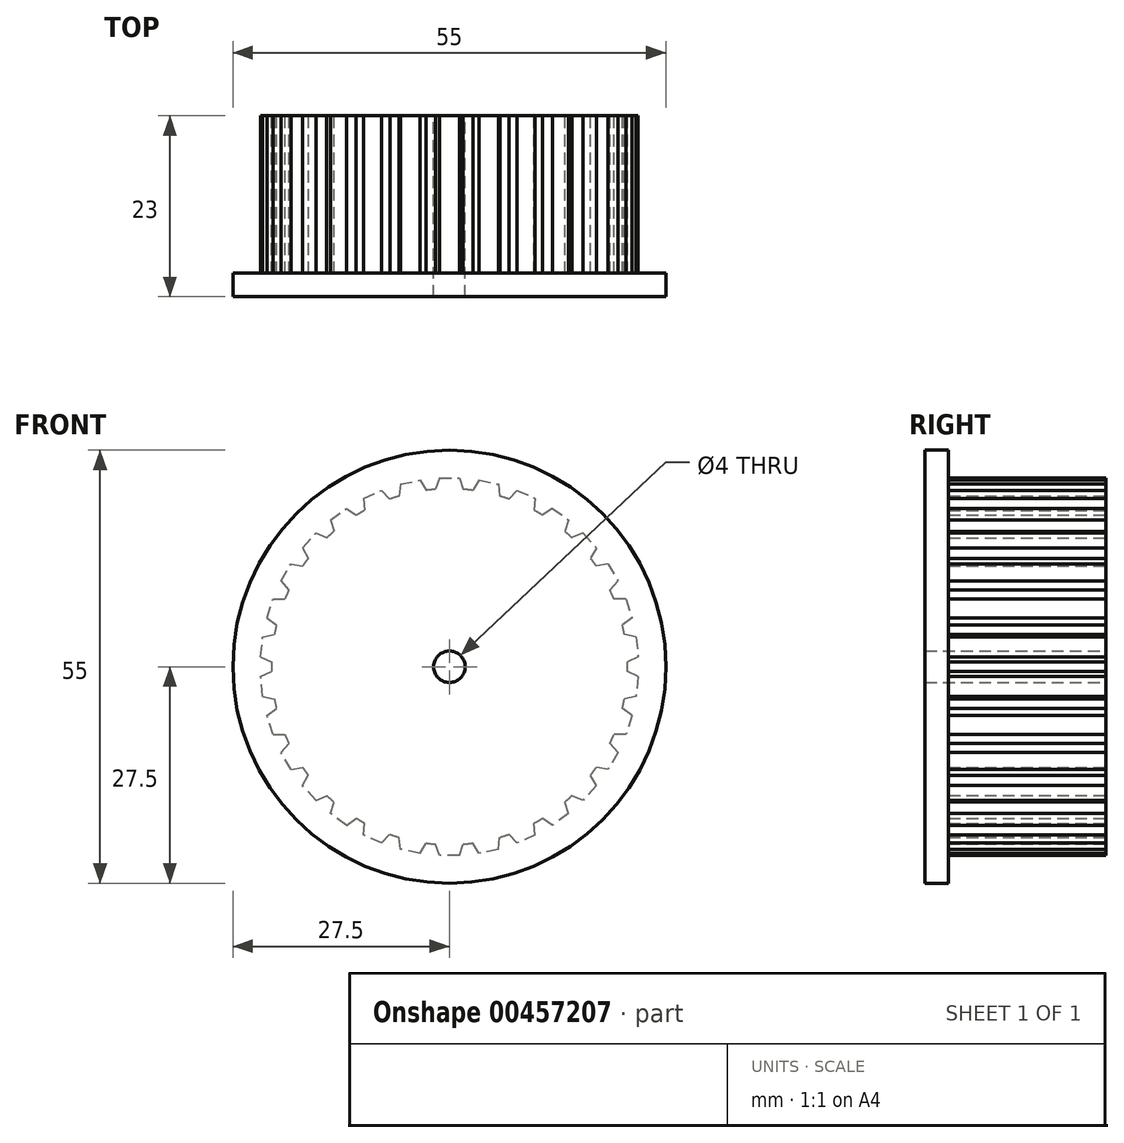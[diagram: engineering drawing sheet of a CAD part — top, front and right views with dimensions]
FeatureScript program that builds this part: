
annotation { "Feature Type Name" : "Feature", "Feature Type Description" : "" }
export const myFeature = defineFeature(function(context is Context, id is Id, definition is map)
    precondition{}
    {
        {
            var Q0;
            Q0=qCreatedBy(makeId("Front.planeOp"),FACE);
            var sketch = newSketch(context, id + "F0", { "sketchPlane" : qUnion([Q0])});
            skCircle(sketch, "E0", {"center": v(0, 0) * mm, "radius": 24 * mm, "construction": true});
            skLineSegment(sketch, "E1", {"start": v(0, 24) * mm, "end": v(0, 22.6) * mm, "construction": true});
            skCircle(sketch, "E2", {"center": v(0, 0) * mm, "radius": 22.6 * mm});
            skLineSegment(sketch, "E3", {"start": v(0, 0) * mm, "end": v(-1.26, 23.97) * mm, "construction": true});
            skLineSegment(sketch, "E4", {"start": v(0, 0) * mm, "end": v(-2.5, 23.87) * mm, "construction": true});
            skLineSegment(sketch, "E5.MirrorCS", {"start": v(0, 0) * mm, "end": v(1.26, 23.97) * mm, "construction": true});
            skLineSegment(sketch, "E6.MirrorCS", {"start": v(0, 0) * mm, "end": v(2.5, 23.87) * mm, "construction": true});
            skLineSegment(sketch, "E7", {"start": v(-1.26, 23.97) * mm, "end": v(1.26, 23.97) * mm});
            skLineSegment(sketch, "E8", {"start": v(-1.26, 23.97) * mm, "end": v(-1.75, 22.53) * mm});
            skLineSegment(sketch, "E9.MirrorCS", {"start": v(1.26, 23.97) * mm, "end": v(1.75, 22.53) * mm});
            skLineSegment(sketch, "E10.1.0", {"start": v(-6.21, 23.18) * mm, "end": v(-6.4, 21.68) * mm});
            skLineSegment(sketch, "E10.1.1", {"start": v(-6.21, 23.18) * mm, "end": v(-3.75, 23.7) * mm});
            skLineSegment(sketch, "E10.1.2", {"start": v(-3.75, 23.7) * mm, "end": v(-2.97, 22.4) * mm});
            skLineSegment(sketch, "E10.2.0", {"start": v(-10.9, 21.38) * mm, "end": v(-10.76, 19.87) * mm});
            skLineSegment(sketch, "E10.2.1", {"start": v(-10.9, 21.38) * mm, "end": v(-8.6, 22.4) * mm});
            skLineSegment(sketch, "E10.2.2", {"start": v(-8.6, 22.4) * mm, "end": v(-7.57, 21.3) * mm});
            skLineSegment(sketch, "E10.3.0", {"start": v(-15.1, 18.65) * mm, "end": v(-14.66, 17.2) * mm});
            skLineSegment(sketch, "E10.3.1", {"start": v(-15.1, 18.65) * mm, "end": v(-13.07, 20.13) * mm});
            skLineSegment(sketch, "E10.3.2", {"start": v(-13.07, 20.13) * mm, "end": v(-11.83, 19.26) * mm});
            skLineSegment(sketch, "E10.4.0", {"start": v(-18.65, 15.1) * mm, "end": v(-17.92, 13.78) * mm});
            skLineSegment(sketch, "E10.4.1", {"start": v(-18.65, 15.1) * mm, "end": v(-16.97, 16.97) * mm});
            skLineSegment(sketch, "E10.4.2", {"start": v(-16.97, 16.97) * mm, "end": v(-15.57, 16.38) * mm});
            skLineSegment(sketch, "E10.5.0", {"start": v(-21.38, 10.9) * mm, "end": v(-20.39, 9.75) * mm});
            skLineSegment(sketch, "E10.5.1", {"start": v(-21.38, 10.9) * mm, "end": v(-20.13, 13.07) * mm});
            skLineSegment(sketch, "E10.5.2", {"start": v(-20.13, 13.07) * mm, "end": v(-18.64, 12.78) * mm});
            skLineSegment(sketch, "E10.6.0", {"start": v(-23.18, 6.21) * mm, "end": v(-21.97, 5.3) * mm});
            skLineSegment(sketch, "E10.6.1", {"start": v(-23.18, 6.21) * mm, "end": v(-22.4, 8.6) * mm});
            skLineSegment(sketch, "E10.6.2", {"start": v(-22.4, 8.6) * mm, "end": v(-20.89, 8.63) * mm});
            skLineSegment(sketch, "E10.7.0", {"start": v(-23.97, 1.26) * mm, "end": v(-22.6, 0.61) * mm});
            skLineSegment(sketch, "E10.7.1", {"start": v(-23.97, 1.26) * mm, "end": v(-23.7, 3.75) * mm});
            skLineSegment(sketch, "E10.7.2", {"start": v(-23.7, 3.75) * mm, "end": v(-22.23, 4.1) * mm});
            skLineSegment(sketch, "E10.8.0", {"start": v(-23.7, -3.75) * mm, "end": v(-22.23, -4.1) * mm});
            skLineSegment(sketch, "E10.8.1", {"start": v(-23.7, -3.75) * mm, "end": v(-23.97, -1.26) * mm});
            skLineSegment(sketch, "E10.8.2", {"start": v(-23.97, -1.26) * mm, "end": v(-22.6, -0.61) * mm});
            skLineSegment(sketch, "E10.9.0", {"start": v(-22.4, -8.6) * mm, "end": v(-20.89, -8.63) * mm});
            skLineSegment(sketch, "E10.9.1", {"start": v(-22.4, -8.6) * mm, "end": v(-23.18, -6.21) * mm});
            skLineSegment(sketch, "E10.9.2", {"start": v(-23.18, -6.21) * mm, "end": v(-21.97, -5.3) * mm});
            skLineSegment(sketch, "E11", {"start": v(0, 0) * mm, "end": v(0, 24) * mm, "construction": true});
            skLineSegment(sketch, "E12.2.10.0", {"start": v(-20.13, -13.07) * mm, "end": v(-18.64, -12.78) * mm});
            skLineSegment(sketch, "E12.3.10.0", {"start": v(-20.13, -13.07) * mm, "end": v(-21.38, -10.9) * mm});
            skLineSegment(sketch, "E12.6.10.0", {"start": v(-21.38, -10.9) * mm, "end": v(-20.39, -9.75) * mm});
            skLineSegment(sketch, "E12.2.11.0", {"start": v(-16.97, -16.97) * mm, "end": v(-15.57, -16.38) * mm});
            skLineSegment(sketch, "E12.3.11.0", {"start": v(-16.97, -16.97) * mm, "end": v(-18.65, -15.1) * mm});
            skLineSegment(sketch, "E12.6.11.0", {"start": v(-18.65, -15.1) * mm, "end": v(-17.92, -13.78) * mm});
            skLineSegment(sketch, "E12.2.12.0", {"start": v(-13.07, -20.13) * mm, "end": v(-11.83, -19.26) * mm});
            skLineSegment(sketch, "E12.3.12.0", {"start": v(-13.07, -20.13) * mm, "end": v(-15.1, -18.65) * mm});
            skLineSegment(sketch, "E12.6.12.0", {"start": v(-15.1, -18.65) * mm, "end": v(-14.66, -17.2) * mm});
            skLineSegment(sketch, "E12.2.13.0", {"start": v(-8.6, -22.4) * mm, "end": v(-7.57, -21.3) * mm});
            skLineSegment(sketch, "E12.3.13.0", {"start": v(-8.6, -22.4) * mm, "end": v(-10.9, -21.38) * mm});
            skLineSegment(sketch, "E12.6.13.0", {"start": v(-10.9, -21.38) * mm, "end": v(-10.76, -19.87) * mm});
            skLineSegment(sketch, "E12.2.14.0", {"start": v(-3.75, -23.7) * mm, "end": v(-2.97, -22.4) * mm});
            skLineSegment(sketch, "E12.3.14.0", {"start": v(-3.75, -23.7) * mm, "end": v(-6.21, -23.18) * mm});
            skLineSegment(sketch, "E12.6.14.0", {"start": v(-6.21, -23.18) * mm, "end": v(-6.4, -21.68) * mm});
            skLineSegment(sketch, "E12.2.15.0", {"start": v(1.26, -23.97) * mm, "end": v(1.75, -22.53) * mm});
            skLineSegment(sketch, "E12.3.15.0", {"start": v(1.26, -23.97) * mm, "end": v(-1.26, -23.97) * mm});
            skLineSegment(sketch, "E12.6.15.0", {"start": v(-1.26, -23.97) * mm, "end": v(-1.75, -22.53) * mm});
            skLineSegment(sketch, "E12.2.16.0", {"start": v(6.21, -23.18) * mm, "end": v(6.4, -21.68) * mm});
            skLineSegment(sketch, "E12.3.16.0", {"start": v(6.21, -23.18) * mm, "end": v(3.75, -23.7) * mm});
            skLineSegment(sketch, "E12.6.16.0", {"start": v(3.75, -23.7) * mm, "end": v(2.97, -22.4) * mm});
            skLineSegment(sketch, "E12.2.17.0", {"start": v(10.9, -21.38) * mm, "end": v(10.76, -19.87) * mm});
            skLineSegment(sketch, "E12.3.17.0", {"start": v(10.9, -21.38) * mm, "end": v(8.6, -22.4) * mm});
            skLineSegment(sketch, "E12.6.17.0", {"start": v(8.6, -22.4) * mm, "end": v(7.57, -21.3) * mm});
            skLineSegment(sketch, "E12.2.18.0", {"start": v(15.1, -18.65) * mm, "end": v(14.66, -17.2) * mm});
            skLineSegment(sketch, "E12.3.18.0", {"start": v(15.1, -18.65) * mm, "end": v(13.07, -20.13) * mm});
            skLineSegment(sketch, "E12.6.18.0", {"start": v(13.07, -20.13) * mm, "end": v(11.83, -19.26) * mm});
            skLineSegment(sketch, "E12.2.19.0", {"start": v(18.65, -15.1) * mm, "end": v(17.92, -13.78) * mm});
            skLineSegment(sketch, "E12.3.19.0", {"start": v(18.65, -15.1) * mm, "end": v(16.97, -16.97) * mm});
            skLineSegment(sketch, "E12.6.19.0", {"start": v(16.97, -16.97) * mm, "end": v(15.57, -16.38) * mm});
            skCircle(sketch, "E13", {"center": v(0, 0) * mm, "radius": 2 * mm});
            skLineSegment(sketch, "E14.2.20.0", {"start": v(21.38, -10.9) * mm, "end": v(20.39, -9.75) * mm});
            skLineSegment(sketch, "E14.3.20.0", {"start": v(21.38, -10.9) * mm, "end": v(20.13, -13.07) * mm});
            skLineSegment(sketch, "E14.6.20.0", {"start": v(20.13, -13.07) * mm, "end": v(18.64, -12.78) * mm});
            skLineSegment(sketch, "E14.2.21.0", {"start": v(23.18, -6.21) * mm, "end": v(21.97, -5.3) * mm});
            skLineSegment(sketch, "E14.3.21.0", {"start": v(23.18, -6.21) * mm, "end": v(22.4, -8.6) * mm});
            skLineSegment(sketch, "E14.6.21.0", {"start": v(22.4, -8.6) * mm, "end": v(20.89, -8.63) * mm});
            skLineSegment(sketch, "E14.2.22.0", {"start": v(23.97, -1.26) * mm, "end": v(22.6, -0.61) * mm});
            skLineSegment(sketch, "E14.3.22.0", {"start": v(23.97, -1.26) * mm, "end": v(23.7, -3.75) * mm});
            skLineSegment(sketch, "E14.6.22.0", {"start": v(23.7, -3.75) * mm, "end": v(22.23, -4.1) * mm});
            skLineSegment(sketch, "E14.2.23.0", {"start": v(23.7, 3.75) * mm, "end": v(22.23, 4.1) * mm});
            skLineSegment(sketch, "E14.3.23.0", {"start": v(23.7, 3.75) * mm, "end": v(23.97, 1.26) * mm});
            skLineSegment(sketch, "E14.6.23.0", {"start": v(23.97, 1.26) * mm, "end": v(22.6, 0.61) * mm});
            skLineSegment(sketch, "E14.2.24.0", {"start": v(22.4, 8.6) * mm, "end": v(20.89, 8.63) * mm});
            skLineSegment(sketch, "E14.3.24.0", {"start": v(22.4, 8.6) * mm, "end": v(23.18, 6.21) * mm});
            skLineSegment(sketch, "E14.6.24.0", {"start": v(23.18, 6.21) * mm, "end": v(21.97, 5.3) * mm});
            skLineSegment(sketch, "E14.2.25.0", {"start": v(20.13, 13.07) * mm, "end": v(18.64, 12.78) * mm});
            skLineSegment(sketch, "E14.3.25.0", {"start": v(20.13, 13.07) * mm, "end": v(21.38, 10.9) * mm});
            skLineSegment(sketch, "E14.6.25.0", {"start": v(21.38, 10.9) * mm, "end": v(20.39, 9.75) * mm});
            skLineSegment(sketch, "E14.2.26.0", {"start": v(16.97, 16.97) * mm, "end": v(15.57, 16.38) * mm});
            skLineSegment(sketch, "E14.3.26.0", {"start": v(16.97, 16.97) * mm, "end": v(18.65, 15.1) * mm});
            skLineSegment(sketch, "E14.6.26.0", {"start": v(18.65, 15.1) * mm, "end": v(17.92, 13.78) * mm});
            skLineSegment(sketch, "E14.2.27.0", {"start": v(13.07, 20.13) * mm, "end": v(11.83, 19.26) * mm});
            skLineSegment(sketch, "E14.3.27.0", {"start": v(13.07, 20.13) * mm, "end": v(15.1, 18.65) * mm});
            skLineSegment(sketch, "E14.6.27.0", {"start": v(15.1, 18.65) * mm, "end": v(14.66, 17.2) * mm});
            skLineSegment(sketch, "E14.2.28.0", {"start": v(8.6, 22.4) * mm, "end": v(7.57, 21.3) * mm});
            skLineSegment(sketch, "E14.3.28.0", {"start": v(8.6, 22.4) * mm, "end": v(10.9, 21.38) * mm});
            skLineSegment(sketch, "E14.6.28.0", {"start": v(10.9, 21.38) * mm, "end": v(10.76, 19.87) * mm});
            skLineSegment(sketch, "E14.2.29.0", {"start": v(3.75, 23.7) * mm, "end": v(2.97, 22.4) * mm});
            skLineSegment(sketch, "E14.3.29.0", {"start": v(3.75, 23.7) * mm, "end": v(6.21, 23.18) * mm});
            skLineSegment(sketch, "E14.6.29.0", {"start": v(6.21, 23.18) * mm, "end": v(6.4, 21.68) * mm});
            skSolve(sketch);
        }
        {
            var Q0;
            Q0=qSketchRegion(id+"F0",true);
            extrude(context, id + "F1", {"entities" : qUnion([Q0]), "depth" : 20 * mm, "offsetDistance" : 25 * mm});
        }
        {
            var Q0;
            Q0=makeQuery(id+"F1.opExtrude","CAP_FACE",FACE,{"disambiguationData":[OSD([sQuery(id+"F0.wireOp",EDGE,"E2"),sQuery(id+"F0.wireOp",EDGE,"E7"),sQuery(id+"F0.wireOp",EDGE,"E8"),sQuery(id+"F0.wireOp",EDGE,"E9.MirrorCS"),sQuery(id+"F0.wireOp",EDGE,"E10.1.0"),sQuery(id+"F0.wireOp",EDGE,"E10.1.1"),sQuery(id+"F0.wireOp",EDGE,"E10.1.2"),sQuery(id+"F0.wireOp",EDGE,"E10.2.0"),sQuery(id+"F0.wireOp",EDGE,"E10.2.1"),sQuery(id+"F0.wireOp",EDGE,"E10.2.2"),sQuery(id+"F0.wireOp",EDGE,"E10.3.0"),sQuery(id+"F0.wireOp",EDGE,"E10.3.1"),sQuery(id+"F0.wireOp",EDGE,"E10.3.2"),sQuery(id+"F0.wireOp",EDGE,"E10.4.0"),sQuery(id+"F0.wireOp",EDGE,"E10.4.1"),sQuery(id+"F0.wireOp",EDGE,"E10.4.2"),sQuery(id+"F0.wireOp",EDGE,"E10.5.0"),sQuery(id+"F0.wireOp",EDGE,"E10.5.1"),sQuery(id+"F0.wireOp",EDGE,"E10.5.2"),sQuery(id+"F0.wireOp",EDGE,"E10.6.0"),sQuery(id+"F0.wireOp",EDGE,"E10.6.1"),sQuery(id+"F0.wireOp",EDGE,"E10.6.2"),sQuery(id+"F0.wireOp",EDGE,"E10.7.0"),sQuery(id+"F0.wireOp",EDGE,"E10.7.1"),sQuery(id+"F0.wireOp",EDGE,"E10.7.2"),sQuery(id+"F0.wireOp",EDGE,"E10.8.0"),sQuery(id+"F0.wireOp",EDGE,"E10.8.1"),sQuery(id+"F0.wireOp",EDGE,"E10.8.2"),sQuery(id+"F0.wireOp",EDGE,"E10.9.0"),sQuery(id+"F0.wireOp",EDGE,"E10.9.1"),sQuery(id+"F0.wireOp",EDGE,"E10.9.2"),sQuery(id+"F0.wireOp",EDGE,"E12.2.10.0"),sQuery(id+"F0.wireOp",EDGE,"E12.3.10.0"),sQuery(id+"F0.wireOp",EDGE,"E12.6.10.0"),sQuery(id+"F0.wireOp",EDGE,"E12.2.11.0"),sQuery(id+"F0.wireOp",EDGE,"E12.3.11.0"),sQuery(id+"F0.wireOp",EDGE,"E12.6.11.0"),sQuery(id+"F0.wireOp",EDGE,"E12.2.12.0"),sQuery(id+"F0.wireOp",EDGE,"E12.3.12.0"),sQuery(id+"F0.wireOp",EDGE,"E12.6.12.0"),sQuery(id+"F0.wireOp",EDGE,"E12.2.13.0"),sQuery(id+"F0.wireOp",EDGE,"E12.3.13.0"),sQuery(id+"F0.wireOp",EDGE,"E12.6.13.0"),sQuery(id+"F0.wireOp",EDGE,"E12.2.14.0"),sQuery(id+"F0.wireOp",EDGE,"E12.3.14.0"),sQuery(id+"F0.wireOp",EDGE,"E12.6.14.0"),sQuery(id+"F0.wireOp",EDGE,"E12.2.15.0"),sQuery(id+"F0.wireOp",EDGE,"E12.3.15.0"),sQuery(id+"F0.wireOp",EDGE,"E12.6.15.0"),sQuery(id+"F0.wireOp",EDGE,"E12.2.16.0"),sQuery(id+"F0.wireOp",EDGE,"E12.3.16.0"),sQuery(id+"F0.wireOp",EDGE,"E12.6.16.0"),sQuery(id+"F0.wireOp",EDGE,"E12.2.17.0"),sQuery(id+"F0.wireOp",EDGE,"E12.3.17.0"),sQuery(id+"F0.wireOp",EDGE,"E12.6.17.0"),sQuery(id+"F0.wireOp",EDGE,"E12.2.18.0"),sQuery(id+"F0.wireOp",EDGE,"E12.3.18.0"),sQuery(id+"F0.wireOp",EDGE,"E12.6.18.0"),sQuery(id+"F0.wireOp",EDGE,"E12.2.19.0"),sQuery(id+"F0.wireOp",EDGE,"E12.3.19.0"),sQuery(id+"F0.wireOp",EDGE,"E12.6.19.0"),sQuery(id+"F0.wireOp",EDGE,"E12.2.20.0"),sQuery(id+"F0.wireOp",EDGE,"E12.3.20.0"),sQuery(id+"F0.wireOp",EDGE,"E12.6.20.0"),sQuery(id+"F0.wireOp",EDGE,"E12.2.21.0"),sQuery(id+"F0.wireOp",EDGE,"E12.3.21.0"),sQuery(id+"F0.wireOp",EDGE,"E12.6.21.0"),sQuery(id+"F0.wireOp",EDGE,"E12.2.22.0"),sQuery(id+"F0.wireOp",EDGE,"E12.3.22.0"),sQuery(id+"F0.wireOp",EDGE,"E12.6.22.0"),sQuery(id+"F0.wireOp",EDGE,"E12.2.23.0"),sQuery(id+"F0.wireOp",EDGE,"E12.3.23.0"),sQuery(id+"F0.wireOp",EDGE,"E12.6.23.0"),sQuery(id+"F0.wireOp",EDGE,"E12.2.24.0"),sQuery(id+"F0.wireOp",EDGE,"E12.3.24.0"),sQuery(id+"F0.wireOp",EDGE,"E12.6.24.0"),sQuery(id+"F0.wireOp",EDGE,"E12.2.25.0"),sQuery(id+"F0.wireOp",EDGE,"E12.3.25.0"),sQuery(id+"F0.wireOp",EDGE,"E12.6.25.0"),sQuery(id+"F0.wireOp",EDGE,"E12.2.26.0"),sQuery(id+"F0.wireOp",EDGE,"E12.3.26.0"),sQuery(id+"F0.wireOp",EDGE,"E12.6.26.0"),sQuery(id+"F0.wireOp",EDGE,"E12.2.27.0"),sQuery(id+"F0.wireOp",EDGE,"E12.3.27.0"),sQuery(id+"F0.wireOp",EDGE,"E12.6.27.0"),sQuery(id+"F0.wireOp",EDGE,"E12.2.28.0"),sQuery(id+"F0.wireOp",EDGE,"E12.3.28.0"),sQuery(id+"F0.wireOp",EDGE,"E12.6.28.0"),sQuery(id+"F0.wireOp",EDGE,"E12.2.29.0"),sQuery(id+"F0.wireOp",EDGE,"E12.3.29.0"),sQuery(id+"F0.wireOp",EDGE,"E12.6.29.0"),sQuery(id+"F0.wireOp",EDGE,"E12.2.30.0"),sQuery(id+"F0.wireOp",EDGE,"E12.3.30.0"),sQuery(id+"F0.wireOp",EDGE,"E12.6.30.0"),sQuery(id+"F0.wireOp",EDGE,"E12.2.31.0"),sQuery(id+"F0.wireOp",EDGE,"E12.3.31.0"),sQuery(id+"F0.wireOp",EDGE,"E12.6.31.0"),sQuery(id+"F0.wireOp",EDGE,"E12.2.32.0"),sQuery(id+"F0.wireOp",EDGE,"E12.3.32.0"),sQuery(id+"F0.wireOp",EDGE,"E12.6.32.0"),sQuery(id+"F0.wireOp",EDGE,"E12.2.33.0"),sQuery(id+"F0.wireOp",EDGE,"E12.3.33.0"),sQuery(id+"F0.wireOp",EDGE,"E12.6.33.0"),sQuery(id+"F0.wireOp",EDGE,"E12.2.34.0"),sQuery(id+"F0.wireOp",EDGE,"E12.3.34.0"),sQuery(id+"F0.wireOp",EDGE,"E12.6.34.0"),sQuery(id+"F0.wireOp",EDGE,"E12.2.35.0"),sQuery(id+"F0.wireOp",EDGE,"E12.3.35.0"),sQuery(id+"F0.wireOp",EDGE,"E12.6.35.0"),sQuery(id+"F0.wireOp",EDGE,"E12.2.36.0"),sQuery(id+"F0.wireOp",EDGE,"E12.3.36.0"),sQuery(id+"F0.wireOp",EDGE,"E12.6.36.0"),sQuery(id+"F0.wireOp",EDGE,"E12.2.37.0"),sQuery(id+"F0.wireOp",EDGE,"E12.3.37.0"),sQuery(id+"F0.wireOp",EDGE,"E12.6.37.0"),sQuery(id+"F0.wireOp",EDGE,"E12.2.38.0"),sQuery(id+"F0.wireOp",EDGE,"E12.3.38.0"),sQuery(id+"F0.wireOp",EDGE,"E12.6.38.0"),sQuery(id+"F0.wireOp",EDGE,"E12.2.39.0"),sQuery(id+"F0.wireOp",EDGE,"E12.3.39.0"),sQuery(id+"F0.wireOp",EDGE,"E12.6.39.0"),sQuery(id+"F0.wireOp",EDGE,"E13")])],"isStart":false});
            var sketch = newSketch(context, id + "F2", { "sketchPlane" : qUnion([Q0])});
            skCircle(sketch, "E15", {"center": v(0, 0) * mm, "radius": 27.5 * mm});
            skCircle(sketch, "E16", {"center": v(0, 0) * mm, "radius": 2 * mm});
            skSolve(sketch);
        }
        {
            var Q0;
            Q0=qSketchRegion(id+"F2",true);
            extrude(context, id + "F3", {"entities" : qUnion([Q0]), "operationType" : NewBodyOperationType.ADD, "depth" : 3 * mm, "offsetDistance" : 25 * mm});
        }
    });
